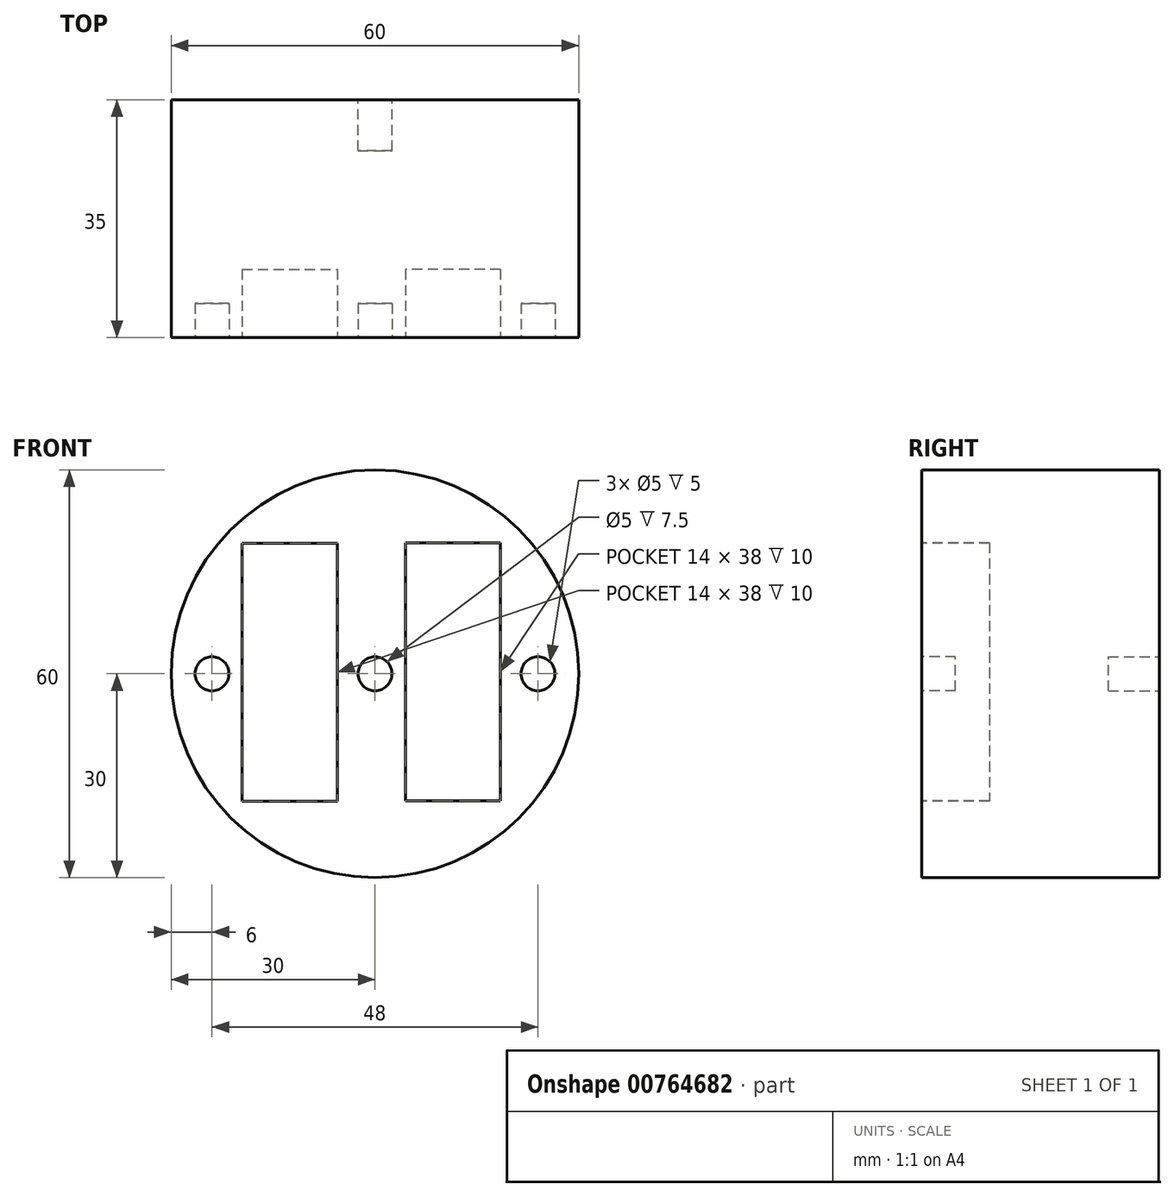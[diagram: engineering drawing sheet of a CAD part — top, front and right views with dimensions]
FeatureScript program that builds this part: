
annotation { "Feature Type Name" : "Feature", "Feature Type Description" : "" }
export const myFeature = defineFeature(function(context is Context, id is Id, definition is map)
    precondition{}
    {
        {
            var Q0;
            Q0=qCreatedBy(makeId("Front.planeOp"),FACE);
            var sketch = newSketch(context, id + "F0", { "sketchPlane" : qUnion([Q0])});
            skCircle(sketch, "E0", {"center": v(0, 0) * mm, "radius": 30 * mm});
            skSolve(sketch);
        }
        {
            var Q0;
            Q0=makeQuery(id+"F0.imprint","IMPRINT",FACE,{"disambiguationData":[TD([[makeQuery(id+"F0.imprint","IMPRINT",EDGE,{"derivedFrom":sQuery(id+"F0.wireOp",EDGE,"E0")}),1.0]])]});
            extrude(context, id + "F1", {"entities" : qUnion([Q0]), "depth" : 35 * mm, "offsetDistance" : 25 * mm});
        }
        {
            var Q0;
            Q0=makeQuery(id+"F1.opExtrude","CAP_FACE",FACE,{"disambiguationData":[OSD([sQuery(id+"F0.wireOp",EDGE,"E0")])],"isStart":true});
            var sketch = newSketch(context, id + "F2", { "sketchPlane" : qUnion([Q0])});
            skPoint(sketch, "E1", {"position": v(0, 0) * mm});
            skSolve(sketch);
        }
        {
            var Q0;
            Q0=makeQuery(id+"F1.opExtrude","CAP_FACE",FACE,{"disambiguationData":[OSD([sQuery(id+"F0.wireOp",EDGE,"E0")])],"isStart":true});
            shell(context, id + "F3", {"entities" : qUnion([Q0]), "thickness" : 27.5 * mm});
        }
        {
            var Q0;
            Q0=makeQuery(id+"F1.opExtrude","CAP_FACE",FACE,{"disambiguationData":[OSD([sQuery(id+"F0.wireOp",EDGE,"E0")])],"isStart":false});
            var sketch = newSketch(context, id + "F4", { "sketchPlane" : qUnion([Q0])});
            skLineSegment(sketch, "E2.bottom", {"start": v(-19.54, 19.23) * mm, "end": v(-5.54, 19.23) * mm});
            skLineSegment(sketch, "E2.top", {"start": v(-19.54, -18.77) * mm, "end": v(-5.54, -18.77) * mm});
            skLineSegment(sketch, "E2.left", {"start": v(-19.54, 19.23) * mm, "end": v(-19.54, -18.77) * mm});
            skLineSegment(sketch, "E2.right", {"start": v(-5.54, 19.23) * mm, "end": v(-5.54, -18.77) * mm});
            skLineSegment(sketch, "E3.bottom", {"start": v(18.46, 19.3) * mm, "end": v(4.46, 19.3) * mm});
            skLineSegment(sketch, "E3.top", {"start": v(18.46, -18.7) * mm, "end": v(4.46, -18.7) * mm});
            skLineSegment(sketch, "E3.left", {"start": v(18.46, 19.3) * mm, "end": v(18.46, -18.7) * mm});
            skLineSegment(sketch, "E3.right", {"start": v(4.46, 19.3) * mm, "end": v(4.46, -18.7) * mm});
            skSolve(sketch);
        }
        {
            var Q0;
            Q0=makeQuery(id+"F4.imprint","IMPRINT",FACE,{"disambiguationData":[TD([[makeQuery(id+"F4.imprint","IMPRINT",EDGE,{"derivedFrom":sQuery(id+"F4.wireOp",EDGE,"E2.bottom")}),-1.0]])]});
            var Q1;
            Q1=makeQuery(id+"F4.imprint","IMPRINT",FACE,{"disambiguationData":[TD([[makeQuery(id+"F4.imprint","IMPRINT",EDGE,{"derivedFrom":sQuery(id+"F4.wireOp",EDGE,"E3.bottom")}),1.0]])]});
            extrude(context, id + "F5", {"entities" : qUnion([Q0, Q1]), "operationType" : NewBodyOperationType.REMOVE, "oppositeDirection" : true, "depth" : 10 * mm, "offsetDistance" : 25 * mm});
        }
        {
            var Q0;
            Q0=makeQuery(id+"F1.opExtrude","CAP_FACE",FACE,{"disambiguationData":[OSD([sQuery(id+"F0.wireOp",EDGE,"E0")])],"isStart":false});
            var sketch = newSketch(context, id + "F6", { "sketchPlane" : qUnion([Q0])});
            skCircle(sketch, "E4", {"center": v(0, 0) * mm, "radius": 2.5 * mm});
            skCircle(sketch, "E5", {"center": v(-24, 0) * mm, "radius": 2.5 * mm});
            skCircle(sketch, "E6", {"center": v(24, 0) * mm, "radius": 2.5 * mm});
            skSolve(sketch);
        }
        {
            var Q0;
            Q0 = qSketchRegion(id + "F6", true);
            extrude(context, id + "F7", {"entities" : qUnion([Q0]), "operationType" : NewBodyOperationType.REMOVE, "oppositeDirection" : true, "depth" : 5 * mm, "offsetDistance" : 25 * mm});
        }
    });
